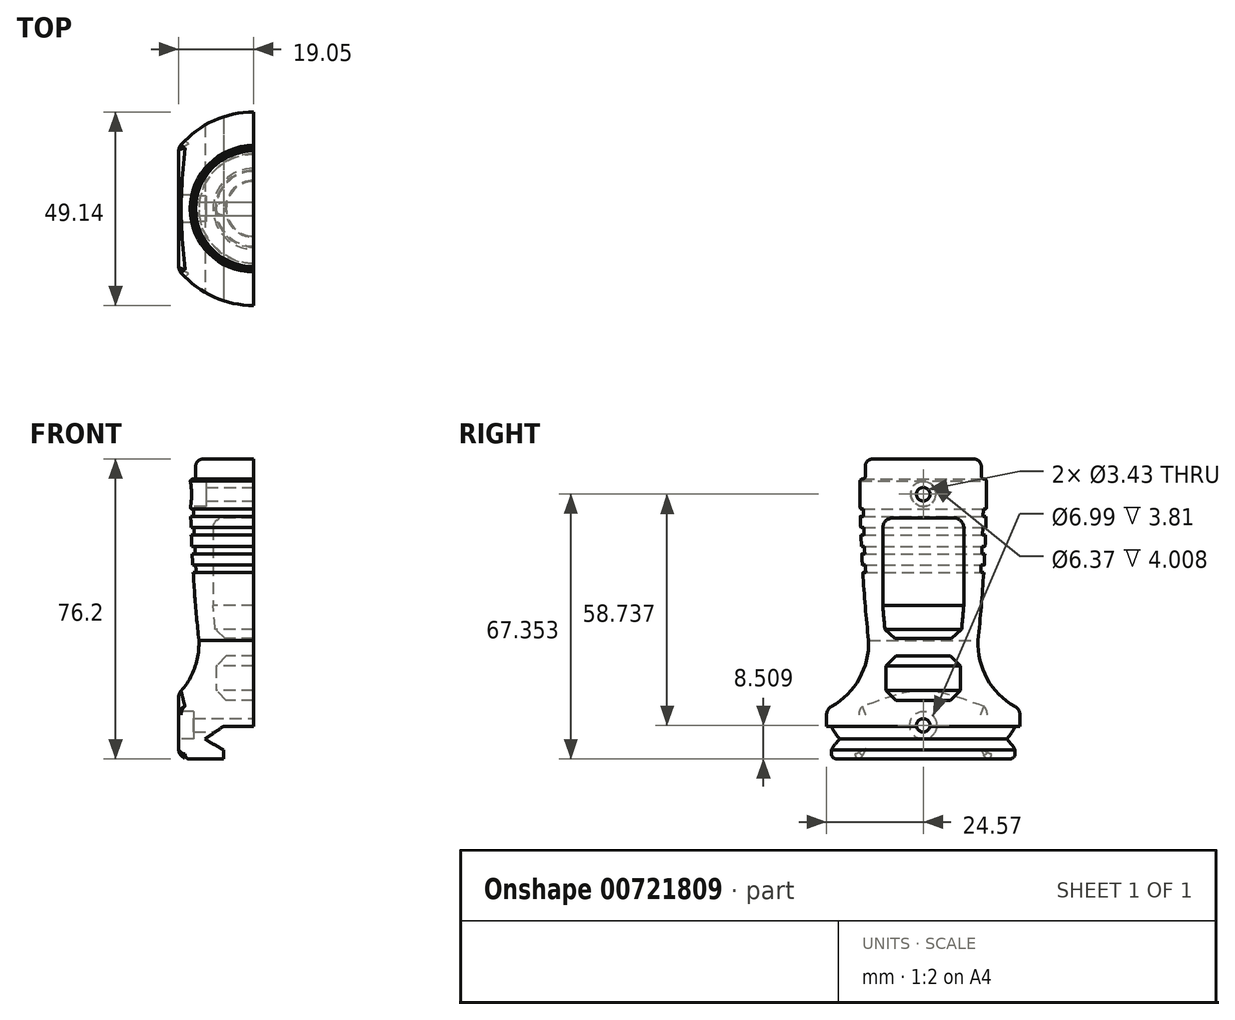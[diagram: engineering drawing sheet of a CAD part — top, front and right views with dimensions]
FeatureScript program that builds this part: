
annotation { "Feature Type Name" : "Feature", "Feature Type Description" : "" }
export const myFeature = defineFeature(function(context is Context, id is Id, definition is map)
    precondition{}
    {
        {
            var Q0;
            Q0=qCreatedBy(makeId("Front.planeOp"),FACE);
            var sketch = newSketch(context, id + "F0", { "sketchPlane" : qUnion([Q0])});
            skLineSegment(sketch, "E0", {"start": v(0, 76.2) * mm, "end": v(12.83, 76.2) * mm});
            skLineSegment(sketch, "E1.0", {"start": v(15.4, 71.12) * mm, "end": v(15.43, 71.12) * mm});
            skLineSegment(sketch, "E2.0", {"start": v(14.73, 71.82) * mm, "end": v(14.73, 74.3) * mm});
            skPoint(sketch, "E3.visualSharp", {"position": v(16.2, 71.12) * mm});
            skArc(sketch, "E3.filletArc", {"start": v(16.07, 70.62) * mm, "mid": v(15.82, 70.98) * mm, "end": v(15.4, 71.12) * mm});
            skPoint(sketch, "E4.visualSharp", {"position": v(14.73, 71.12) * mm});
            skArc(sketch, "E4.filletArc", {"start": v(14.73, 71.82) * mm, "mid": v(14.94, 71.32) * mm, "end": v(15.43, 71.12) * mm});
            skPoint(sketch, "E5.visualSharp", {"position": v(14.73, 76.2) * mm});
            skArc(sketch, "E5.filletArc", {"start": v(14.73, 74.3) * mm, "mid": v(14.17, 75.64) * mm, "end": v(12.83, 76.2) * mm});
            skArc(sketch, "E6", {"start": v(13.9, 30.14) * mm, "mid": v(14.73, 38.71) * mm, "end": v(15.36, 47.3) * mm});
            skPoint(sketch, "E7.orphan", {"position": v(16.2, 0) * mm});
            skLineSegment(sketch, "E8.0", {"start": v(15.24, 63.5) * mm, "end": v(15.76, 63.5) * mm});
            skLineSegment(sketch, "E9.0", {"start": v(15.2, 61.6) * mm, "end": v(15.97, 61.6) * mm});
            skLineSegment(sketch, "E10.0", {"start": v(15.12, 58.74) * mm, "end": v(15.89, 58.74) * mm});
            skLineSegment(sketch, "E11.0", {"start": v(15.06, 56.83) * mm, "end": v(15.82, 56.83) * mm});
            skLineSegment(sketch, "E12.0", {"start": v(14.94, 53.98) * mm, "end": v(15.7, 53.98) * mm});
            skLineSegment(sketch, "E13.0", {"start": v(14.86, 52.07) * mm, "end": v(15.62, 52.07) * mm});
            skLineSegment(sketch, "E14.0", {"start": v(14.7, 49.21) * mm, "end": v(15.47, 49.21) * mm});
            skLineSegment(sketch, "E15.0", {"start": v(14.6, 47.3) * mm, "end": v(15.36, 47.3) * mm});
            skArc(sketch, "E16.0", {"start": v(14.6, 47.3) * mm, "mid": v(14.65, 48.26) * mm, "end": v(14.7, 49.21) * mm});
            skArc(sketch, "E17.trimOffspring", {"start": v(16.01, 63.75) * mm, "mid": v(16.06, 67.18) * mm, "end": v(16.07, 70.62) * mm});
            skArc(sketch, "E18.trimOffspring", {"start": v(15.2, 61.6) * mm, "mid": v(15.22, 62.55) * mm, "end": v(15.24, 63.5) * mm});
            skArc(sketch, "E19.trimOffspring", {"start": v(15.89, 58.74) * mm, "mid": v(15.93, 60.17) * mm, "end": v(15.97, 61.6) * mm});
            skArc(sketch, "E20.trimOffspring", {"start": v(15.06, 56.83) * mm, "mid": v(15.1, 57.78) * mm, "end": v(15.12, 58.74) * mm});
            skArc(sketch, "E21.trimOffspring", {"start": v(15.7, 53.98) * mm, "mid": v(15.77, 55.4) * mm, "end": v(15.82, 56.83) * mm});
            skArc(sketch, "E22.trimOffspring", {"start": v(14.86, 52.07) * mm, "mid": v(14.9, 53.02) * mm, "end": v(14.94, 53.98) * mm});
            skArc(sketch, "E23.trimOffspring", {"start": v(15.47, 49.21) * mm, "mid": v(15.55, 50.64) * mm, "end": v(15.62, 52.07) * mm});
            skPoint(sketch, "E24.visualSharp", {"position": v(16, 63.5) * mm});
            skArc(sketch, "E24.filletArc", {"start": v(15.76, 63.5) * mm, "mid": v(15.93, 63.57) * mm, "end": v(16.01, 63.75) * mm});
            skLineSegment(sketch, "E25", {"start": v(0, 0) * mm, "end": v(23.3, 0) * mm});
            skLineSegment(sketch, "E26", {"start": v(24.57, 1.27) * mm, "end": v(24.57, 11.14) * mm});
            skArc(sketch, "E27", {"start": v(13.9, 30.14) * mm, "mid": v(16.2, 20.42) * mm, "end": v(23.27, 13.36) * mm});
            skPoint(sketch, "E28.visualSharp", {"position": v(24.57, 12.7) * mm});
            skArc(sketch, "E28.filletArc", {"start": v(24.57, 11.14) * mm, "mid": v(24.22, 12.43) * mm, "end": v(23.27, 13.36) * mm});
            skPoint(sketch, "E29.visualSharp", {"position": v(24.57, 0) * mm});
            skArc(sketch, "E29.filletArc", {"start": v(23.3, 0) * mm, "mid": v(24.2, 0.37) * mm, "end": v(24.57, 1.27) * mm});
            skLineSegment(sketch, "E30.0", {"start": v(10.29, 38.93) * mm, "end": v(10.29, 58.67) * mm});
            skArc(sketch, "E31.0", {"start": v(9.49, 30.6) * mm, "mid": v(9.91, 34.77) * mm, "end": v(10.29, 38.93) * mm});
            skLineSegment(sketch, "E32", {"start": v(9.49, 30.6) * mm, "end": v(0, 30.6) * mm});
            skLineSegment(sketch, "E33.0", {"start": v(9.49, 26.16) * mm, "end": v(0, 26.16) * mm});
            skLineSegment(sketch, "E34", {"start": v(9.49, 26.16) * mm, "end": v(9.49, 14.86) * mm});
            skLineSegment(sketch, "E35", {"start": v(9.49, 14.86) * mm, "end": v(0, 14.86) * mm});
            skLineSegment(sketch, "E36.trimOffspring", {"start": v(0, 26.16) * mm, "end": v(0, 30.6) * mm});
            skLineSegment(sketch, "E37.trimOffspring", {"start": v(0, 61.21) * mm, "end": v(0, 76.2) * mm});
            skLineSegment(sketch, "E38", {"start": v(0, 14.86) * mm, "end": v(0, 0) * mm});
            skLineSegment(sketch, "E39.0", {"start": v(0, 61.21) * mm, "end": v(7.75, 61.21) * mm});
            skPoint(sketch, "E40.visualSharp", {"position": v(10.29, 61.21) * mm});
            skArc(sketch, "E40.filletArc", {"start": v(10.29, 58.67) * mm, "mid": v(9.54, 60.47) * mm, "end": v(7.75, 61.21) * mm});
            skSolve(sketch);
        }
        {
            var Q0;
            Q0=makeQuery(id+"F0.imprint","IMPRINT",FACE,{"disambiguationData":[TD([[makeQuery(id+"F0.imprint","IMPRINT",EDGE,{"derivedFrom":sQuery(id+"F0.wireOp",EDGE,"E0")}),-1.0]])]});
            var Q1;
            Q1=sQuery(id+"F0.wireOp",EDGE,"E37.trimOffspring");
            revolve(context, id + "F1", {"surfaceOperationType" : NewSurfaceOperationType.NEW, "entities" : qUnion([Q0]), "axis" : qUnion([Q1]), "revolveType" : RevolveType.FULL});
        }
        {
            var Q0;
            Q0=qCreatedBy(makeId("Front.planeOp"),FACE);
            var sketch = newSketch(context, id + "F2", { "sketchPlane" : qUnion([Q0])});
            skLineSegment(sketch, "E41.0", {"start": v(19.05, 0) * mm, "end": v(19.05, 22.93) * mm});
            skLineSegment(sketch, "E42.0", {"start": v(-19.05, 0) * mm, "end": v(-19.05, 22.93) * mm});
            skLineSegment(sketch, "E43", {"start": v(0, 0) * mm, "end": v(0, 22.93) * mm});
            skLineSegment(sketch, "E44.0", {"start": v(7.68, 0) * mm, "end": v(7.68, 2.29) * mm});
            skLineSegment(sketch, "E45", {"start": v(7.68, 0) * mm, "end": v(19.05, 0) * mm});
            skLineSegment(sketch, "E46.0", {"start": v(0, 8.26) * mm, "end": v(7.68, 8.26) * mm});
            skLineSegment(sketch, "E47", {"start": v(7.68, 2.29) * mm, "end": v(12.38, 5.02) * mm});
            skLineSegment(sketch, "E48", {"start": v(12.38, 5.02) * mm, "end": v(7.68, 8.26) * mm});
            skLineSegment(sketch, "E49.MirrorCS", {"start": v(0, 8.26) * mm, "end": v(-7.68, 8.26) * mm});
            skLineSegment(sketch, "E50.MirrorCS", {"start": v(-12.38, 5.02) * mm, "end": v(-7.68, 8.26) * mm});
            skLineSegment(sketch, "E51.MirrorCS", {"start": v(-7.68, 2.29) * mm, "end": v(-12.38, 5.02) * mm});
            skLineSegment(sketch, "E52.MirrorCS", {"start": v(-7.68, 0) * mm, "end": v(-7.68, 2.29) * mm});
            skPoint(sketch, "E53.orphan", {"position": v(7.68, 5.02) * mm});
            skPoint(sketch, "E54.orphan", {"position": v(-7.68, 5.02) * mm});
            skLineSegment(sketch, "E55", {"start": v(-7.68, 0) * mm, "end": v(-19.05, 0) * mm});
            skLineSegment(sketch, "E56", {"start": v(-19.05, 22.93) * mm, "end": v(-34.37, 22.93) * mm});
            skLineSegment(sketch, "E57", {"start": v(-34.37, 22.93) * mm, "end": v(-34.37, -12.19) * mm});
            skLineSegment(sketch, "E58", {"start": v(-34.37, -12.19) * mm, "end": v(36.04, -12.19) * mm});
            skLineSegment(sketch, "E59", {"start": v(36.04, -12.19) * mm, "end": v(36.04, 22.93) * mm});
            skLineSegment(sketch, "E60", {"start": v(36.04, 22.93) * mm, "end": v(19.05, 22.93) * mm});
            skSolve(sketch);
        }
        {
            var Q0;
            Q0=makeQuery(id+"F2.imprint","IMPRINT",FACE,{"disambiguationData":[TD([[makeQuery(id+"F2.imprint","IMPRINT",EDGE,{"derivedFrom":sQuery(id+"F2.wireOp",EDGE,"E41.0")}),-1.0]])]});
            extrude(context, id + "F3", {"entities" : qUnion([Q0]), "operationType" : NewBodyOperationType.REMOVE, "endBound" : BoundingType.SYMMETRIC, "oppositeDirection" : true, "depth" : 50.8 * mm, "offsetDistance" : 25.4 * mm});
        }
        {
            var Q0;
            Q0=makeQuery(id+"F3.boolean.opBoolean","INTERSECT",EDGE,{"derivedFrom":[makeQuery(id+"F1.opRevolve","SWEPT_FACE",FACE,{"disambiguationData":[OSD([sQuery(id+"F0.wireOp",EDGE,"E27")])]}),makeQuery(id+"F3.opExtrude","SWEPT_FACE",FACE,{"disambiguationData":[OSD([sQuery(id+"F2.wireOp",EDGE,"E41.0")])]})]});
            var Q1;
            Q1=makeQuery(id+"F3.boolean.opBoolean","INTERSECT",EDGE,{"derivedFrom":[makeQuery(id+"F1.opRevolve","SWEPT_FACE",FACE,{"disambiguationData":[OSD([sQuery(id+"F0.wireOp",EDGE,"E27")])]}),makeQuery(id+"F3.opExtrude","SWEPT_FACE",FACE,{"disambiguationData":[OSD([sQuery(id+"F2.wireOp",EDGE,"E42.0")])]})]});
            var Q2;
            Q2=makeQuery(id+"F3.boolean.opBoolean","INTERSECT",EDGE,{"disambiguationData":[OD(0.0)],"derivedFrom":[makeQuery(id+"F1.opRevolve","SWEPT_FACE",FACE,{"disambiguationData":[OSD([sQuery(id+"F0.wireOp",EDGE,"E26")])]}),makeQuery(id+"F3.opExtrude","SWEPT_FACE",FACE,{"disambiguationData":[OSD([sQuery(id+"F2.wireOp",EDGE,"E42.0")])]})]});
            fillet(context, id + "F4", {"entities" : qUnion([Q0, Q1, Q2]), "radius" : 2.54 * mm, "tangentPropagation" : true, "allowEdgeOverflow" : false});
        }
        {
            var Q0;
            Q0=qCreatedBy(makeId("Right.planeOp"),FACE);
            var sketch = newSketch(context, id + "F5", { "sketchPlane" : qUnion([Q0])});
            skCircle(sketch, "E61", {"center": v(0, 8.5) * mm, "radius": 1.71 * mm});
            skCircle(sketch, "E62", {"center": v(0, 67.25) * mm, "radius": 1.71 * mm});
            skSolve(sketch);
        }
        {
            var Q0;
            Q0 = qSketchRegion(id + "F5", true);
            extrude(context, id + "F6", {"entities" : qUnion([Q0]), "operationType" : NewBodyOperationType.REMOVE, "endBound" : BoundingType.SYMMETRIC, "oppositeDirection" : true, "depth" : 76.2 * mm, "offsetDistance" : 25.4 * mm});
        }
        {
            var Q0;
            Q0=makeQuery(id+"F3.boolean.opBoolean","COPY",FACE,{"derivedFrom":makeQuery(id+"F3.opExtrude","SWEPT_FACE",FACE,{"disambiguationData":[OSD([sQuery(id+"F2.wireOp",EDGE,"E42.0")])]})});
            var sketch = newSketch(context, id + "F7", { "sketchPlane" : qUnion([Q0])});
            skCircle(sketch, "E63", {"center": v(0, 8.5) * mm, "radius": 3.5 * mm});
            skSolve(sketch);
        }
        {
            var Q0;
            Q0 = qSketchRegion(id + "F7", true);
            extrude(context, id + "F8", {"entities" : qUnion([Q0]), "operationType" : NewBodyOperationType.REMOVE, "oppositeDirection" : true, "depth" : 3.8 * mm, "offsetDistance" : 25.4 * mm});
        }
        {
            var Q0;
            Q0=makeQuery(id+"F3.boolean.opBoolean","COPY",FACE,{"derivedFrom":makeQuery(id+"F3.opExtrude","SWEPT_FACE",FACE,{"disambiguationData":[OSD([sQuery(id+"F2.wireOp",EDGE,"E42.0")])]})});
            var sketch = newSketch(context, id + "F9", { "sketchPlane" : qUnion([Q0])});
            skCircle(sketch, "E64", {"center": v(0, 67.35) * mm, "radius": 3.19 * mm});
            skSolve(sketch);
        }
        {
            var Q0;
            Q0 = qSketchRegion(id + "F9", true);
            extrude(context, id + "F10", {"entities" : qUnion([Q0]), "operationType" : NewBodyOperationType.REMOVE, "oppositeDirection" : true, "depth" : 7 * mm, "offsetDistance" : 25.4 * mm});
        }
        {
            var Q0;
            Q0=qCreatedBy(makeId("Front.planeOp"),FACE);
            var sketch = newSketch(context, id + "F11", { "sketchPlane" : qUnion([Q0])});
            skLineSegment(sketch, "E65", {"start": v(28.96, 79.63) * mm, "end": v(0, 79.63) * mm});
            skLineSegment(sketch, "E66", {"start": v(28.96, 79.63) * mm, "end": v(28.96, -7.73) * mm});
            skLineSegment(sketch, "E67", {"start": v(0, -7.73) * mm, "end": v(28.96, -7.73) * mm});
            skLineSegment(sketch, "E68", {"start": v(0, -7.73) * mm, "end": v(0, 79.63) * mm});
            skSolve(sketch);
        }
        {
            var Q0;
            Q0 = qSketchRegion(id + "F11", true);
            extrude(context, id + "F12", {"entities" : qUnion([Q0]), "operationType" : NewBodyOperationType.REMOVE, "endBound" : BoundingType.SYMMETRIC, "depth" : 76.2 * mm, "offsetDistance" : 25.4 * mm});
        }
        {
            var Q0;
            Q0=makeQuery(id+"F1.opRevolve","SWEPT_EDGE",EDGE,{"disambiguationData":[OSD([sQuery(id+"F0.wireOp",EDGE,"E33.0"),sQuery(id+"F0.wireOp",EDGE,"E34")])]});
            var Q1;
            Q1=makeQuery(id+"F1.opRevolve","SWEPT_EDGE",EDGE,{"disambiguationData":[OSD([sQuery(id+"F0.wireOp",EDGE,"E31.0"),sQuery(id+"F0.wireOp",EDGE,"E32")])]});
            var Q2;
            Q2=makeQuery(id+"F1.opRevolve","SWEPT_EDGE",EDGE,{"disambiguationData":[OSD([sQuery(id+"F0.wireOp",EDGE,"E34"),sQuery(id+"F0.wireOp",EDGE,"E35")])]});
            chamfer(context, id + "F13", {"entities" : qUnion([Q0, Q1, Q2]), "width" : 2.54 * mm, "tangentPropagation" : true});
        }
    });
